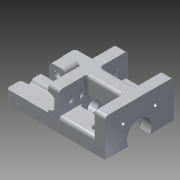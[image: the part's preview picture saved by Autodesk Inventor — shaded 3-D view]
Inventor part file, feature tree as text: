
AUTODESK INVENTOR PART (.ipt)
format: ipt  version: 2015 SP1 (Build 190203100, 203)  size: 643,072 bytes
history: native  units: mm
features: sketch x23, extrude x20, fillet x13, projected_geometry x10, reference x8, hole x3, mirror x1, plane x1, other x1, revolve x1
ambient origin geometry x8: Origin, YZ Plane, XZ Plane, XY Plane, X Axis, Y Axis, Z Axis, Center Point
bodies: Solid1 (feature_tree)
feature tree (81):
  extrude  "Extrusion1"  Depth=12.0mm
  extrude  "Extrusion2"  Depth=10.0mm
  extrude  "Extrusion3"  Depth=25.0mm TaperAngle=0.0deg
  extrude  "Extrusion4"  Depth=16.0mm TaperAngle=0.0deg
  extrude  "Extrusion5"  Depth=24.0mm TaperAngle=0.0deg
  extrude  "Extrusion6"  Depth=2.0mm
  extrude  "Extrusion7"  Depth=4.0mm
  mirror  "Mirror1"
  plane  "Work Plane1"
  extrude  "Extrusion9"  Depth=4.0mm
  sketch  "Sketch8"  dims[d19=4.0mm d20=4.0mm]
  other  "Work Axis1"
  revolve  "Revolution1"  [1 undecoded]
  fillet  "Fillet9"  Radius=2.0mm
  fillet  "Fillet11"  Radius=1.75mm
  extrude  "Extrusion18"  Depth=10.0mm TaperAngle=0.0deg
  extrude  "Extrusion19"  Depth=1.75mm
  extrude  "Extrusion20"  Depth=10.0mm TaperAngle=0.0deg
  fillet  "Fillet13"  Radius=5.0mm
  fillet  "Fillet12"  Radius=5.0mm
  extrude  "Extrusion21"  Depth=1.5mm
  extrude  "Extrusion22"  Depth=10.0mm
  extrude  "Extrusion23"  Depth=22.2mm
  fillet  "Fillet15"  Radius=8.0mm
  fillet  "Fillet16"  Radius=10.5mm
  fillet  "Fillet17"  Radius=8.0mm
  fillet  "Fillet18"  Radius=2.0mm
  hole  "Hole1"  [1 undecoded]
  extrude  "Extrusion25"  Depth=15.5mm
  extrude  "Extrusion26"  Depth=3.0mm TaperAngle=0.0deg
  fillet  "Fillet19"  Radius=2.0mm
  fillet  "Fillet20"  Radius=3.0mm
  hole  "Hole2"  [1 undecoded]
  hole  "Hole3"  [1 undecoded]
  fillet  "Fillet21"  Radius=19.0mm
  extrude  "Extrusion27"  Depth=14.0mm
  fillet  "Fillet23"  Radius=19.0mm
  extrude  "Extrusion33"  Depth=14.0mm
  extrude  "Extrusion34"  Depth=10.0mm TaperAngle=0.0deg
  fillet  "Fillet26"  Radius=3.0mm
  extrude  "Extrusion36"  Depth=3.0mm
  sketch  "Sketch1"  dims[d0=66.0mm d1=12.0mm]
  sketch  "Sketch2"  dims[d2=10.0mm d3=0.0mm d4=14.0mm]
  sketch  "Sketch3"  dims[d5=14.0mm d6=25.0mm d7=0.0mm]
  reference  "Reference1"
  reference  "Reference2"
  sketch  "Sketch4"  dims[d8=25.0mm d9=0.0mm d10=16.0mm d11=0.0mm]
  projected_geometry  "Projected Loop1"
  sketch  "Sketch6"  dims[d13=10.5mm d14=24.0mm d15=0.0mm]
  sketch  "Sketch7"  dims[d16=20.0mm d17=0.0mm d18=2.0mm]
  reference  "Reference4"
  sketch  "Sketch9"  dims[d21=4.0mm d22=4.0mm]
  sketch  "Sketch11"  dims[d23=6.0mm d24=6.0mm d25=2.0mm d26=1.75mm]
  sketch  "Sketch17"  dims[d27=10.0mm d28=5.0mm d29=0.0mm]
  sketch  "Sketch20"  dims[d30=-29.0mm d35=1.75mm]
  sketch  "Sketch21"  dims[d36=10.0mm d37=8.0mm d38=0.0mm d39=5.0mm d40=5.0mm]
  projected_geometry  "Projected Loop3"
  sketch  "Sketch22"  dims[d41=90.0deg d71=1.5mm]
  projected_geometry  "Projected Loop4"
  projected_geometry  "Projected Loop5"
  sketch  "Sketch23"  dims[d73=3.0mm d76=10.0mm]
  projected_geometry  "Projected Loop6"
  sketch  "Sketch25"  dims[d84=18.0mm d85=0.0mm d86=22.2mm d87=8.0mm d88=0.0mm d89=10.5mm d90=8.0mm d91=0.0mm d92=2.0mm]
  projected_geometry  "Projected Loop8"
  sketch  "Sketch27"  dims[d93=0.75mm d94=18.0mm d95=0.0mm]
  reference  "Reference8"
  sketch  "Sketch28"  dims[d97=18.0mm d98=0.0mm d99=15.5mm]
  projected_geometry  "Projected Loop9"
  reference  "Reference9"
  sketch  "Sketch29"  dims[d100=14.0mm d101=17.0mm d102=0.0mm d106=2.0mm d107=3.0mm]
  projected_geometry  "Projected Loop10"
  sketch  "Sketch31"  dims[d108=4.0mm d109=10.0mm]
  reference  "Reference12"
  reference  "Reference13"
  sketch  "Sketch32"  dims[d110=6.0mm d111=6.0mm d112=4.0mm d113=2.0mm d114=90.0deg d115=8.0mm d116=20.594885mm d117=14.0mm d118=19.0mm]
  sketch  "Sketch39"  dims[d119=24.0mm d120=14.0mm d121=19.0mm]
  projected_geometry  "Projected Loop14"
  sketch  "Sketch40"  dims[d122=16.0mm d123=14.0mm]
  projected_geometry  "Projected Loop15"
  sketch  "Sketch43"  dims[d124=44.0mm d125=0.0mm d126=10.0mm d127=0.0mm d128=3.0mm d129=3.0mm d130=3.2mm d131=6.0mm d132=6.0mm d133=4.0mm d134=90.0deg d135=8.0mm d136=20.594885mm d137=1.0mm d138=3.2mm d139=6.0mm d140=6.0mm d141=3.0mm d142=90.0deg d143=8.0mm d144=20.594885mm d145=7.9mm d146=4.5mm d147=0.0mm d152=3.0mm d175=2.0mm d176=1.0mm d177=0.0mm d178=1.0mm d179=0.0mm d185=1.0mm d186=10.0mm d187=0.0mm]
  reference  "Reference14"
note: 4 required parameter values undecoded (feature->parameter linkage not recoverable at this tier; creation-order binding heuristic only, values carry confidence <= 0.55)